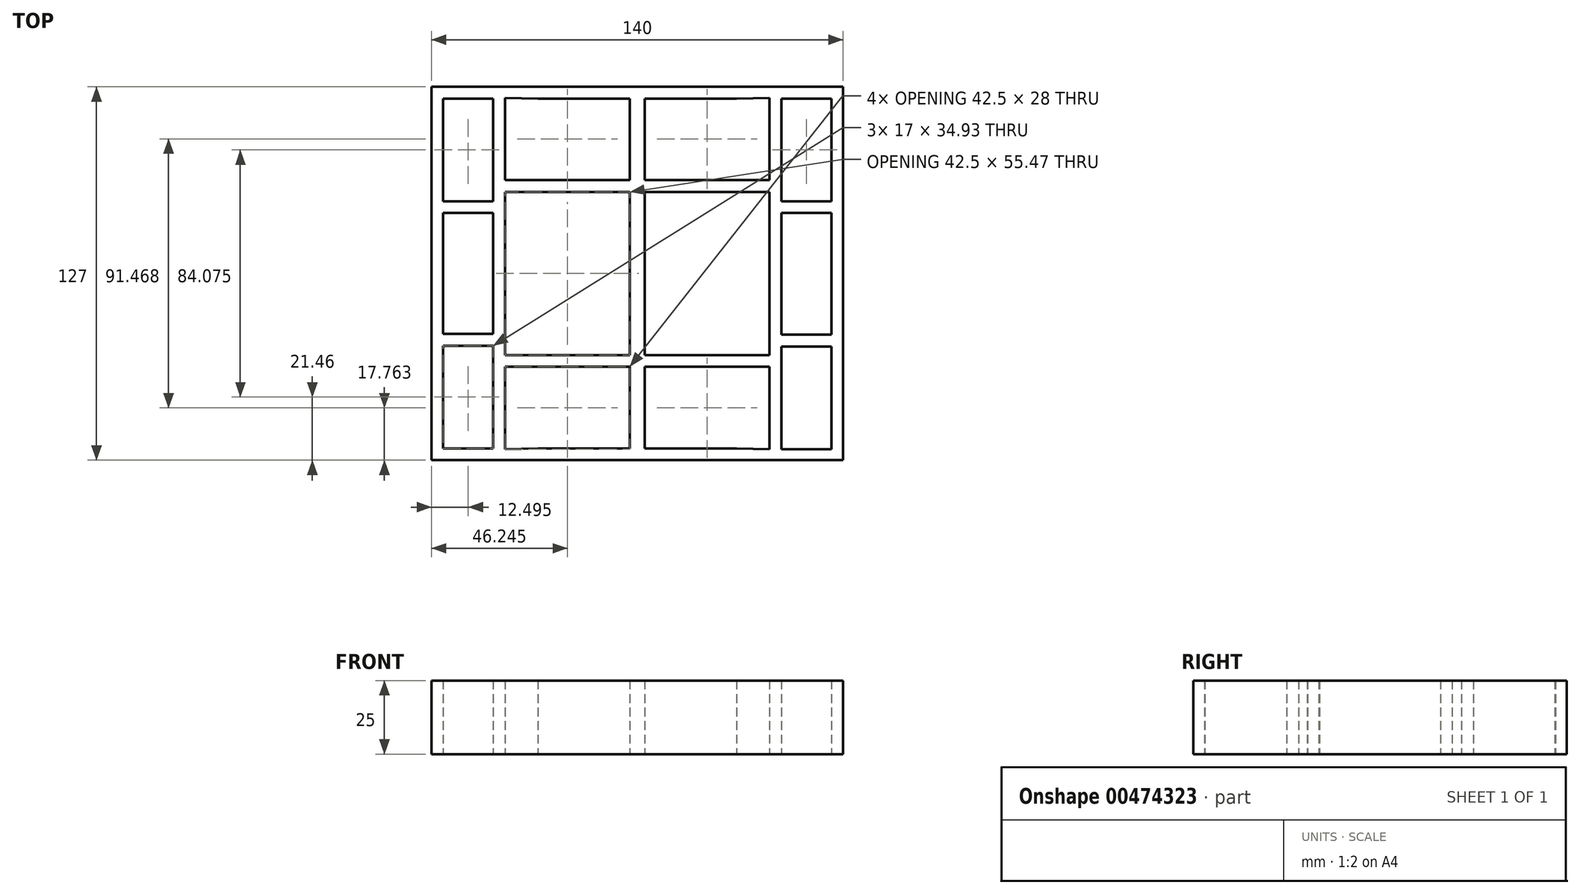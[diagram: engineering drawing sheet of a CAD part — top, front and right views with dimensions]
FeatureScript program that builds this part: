
annotation { "Feature Type Name" : "Feature", "Feature Type Description" : "" }
export const myFeature = defineFeature(function(context is Context, id is Id, definition is map)
    precondition{}
    {
        {
            var Q0;
            Q0=qCreatedBy(makeId("Top.planeOp"),FACE);
            var sketch = newSketch(context, id + "F0", { "sketchPlane" : qUnion([Q0])});
            skLineSegment(sketch, "E0", {"start": v(54.18, 45.65) * mm, "end": v(-85.82, 45.65) * mm});
            skLineSegment(sketch, "E1", {"start": v(-85.82, 45.65) * mm, "end": v(-85.82, -81.35) * mm});
            skLineSegment(sketch, "E2", {"start": v(54.18, -81.35) * mm, "end": v(-85.82, -81.35) * mm});
            skLineSegment(sketch, "E3", {"start": v(54.18, 45.65) * mm, "end": v(54.18, -81.35) * mm});
            skLineSegment(sketch, "E4", {"start": v(50.18, 41.65) * mm, "end": v(33.18, 41.65) * mm});
            skLineSegment(sketch, "E5", {"start": v(-81.82, -77.35) * mm, "end": v(-64.82, -77.35) * mm});
            skLineSegment(sketch, "E6", {"start": v(-81.82, 41.65) * mm, "end": v(-64.82, 41.65) * mm});
            skLineSegment(sketch, "E7", {"start": v(33.18, -77.59) * mm, "end": v(50.18, -77.59) * mm});
            skLineSegment(sketch, "E8", {"start": v(50.18, -10.85) * mm, "end": v(50.18, -24.85) * mm});
            skLineSegment(sketch, "E9", {"start": v(33.18, -10.85) * mm, "end": v(33.18, -24.85) * mm});
            skLineSegment(sketch, "E10", {"start": v(29.18, -10.85) * mm, "end": v(29.18, -24.85) * mm});
            skLineSegment(sketch, "E11", {"start": v(-13.32, -15.85) * mm, "end": v(-13.32, -19.85) * mm});
            skLineSegment(sketch, "E12", {"start": v(-18.32, -15.85) * mm, "end": v(-18.32, -19.85) * mm});
            skLineSegment(sketch, "E13", {"start": v(-60.82, -10.85) * mm, "end": v(-60.82, -24.85) * mm});
            skLineSegment(sketch, "E14", {"start": v(-64.82, -10.85) * mm, "end": v(-64.82, -24.85) * mm});
            skLineSegment(sketch, "E15", {"start": v(-81.82, -10.85) * mm, "end": v(-81.82, -24.85) * mm});
            skLineSegment(sketch, "E16", {"start": v(29.18, -77.59) * mm, "end": v(29.18, -49.59) * mm});
            skLineSegment(sketch, "E17", {"start": v(29.18, 41.88) * mm, "end": v(29.18, 13.88) * mm});
            skLineSegment(sketch, "E18", {"start": v(-60.82, 41.88) * mm, "end": v(-60.82, 13.88) * mm});
            skLineSegment(sketch, "E19", {"start": v(-60.82, -77.59) * mm, "end": v(-60.82, -49.59) * mm});
            skLineSegment(sketch, "E20", {"start": v(29.18, -49.59) * mm, "end": v(-13.32, -49.59) * mm});
            skLineSegment(sketch, "E21", {"start": v(29.18, -24.85) * mm, "end": v(29.18, -45.59) * mm});
            skLineSegment(sketch, "E22", {"start": v(29.18, -45.59) * mm, "end": v(-13.32, -45.59) * mm});
            skLineSegment(sketch, "E23", {"start": v(-13.32, -19.85) * mm, "end": v(-13.32, -45.59) * mm});
            skLineSegment(sketch, "E24", {"start": v(-13.32, -49.59) * mm, "end": v(-13.32, -61.31) * mm});
            skLineSegment(sketch, "E25", {"start": v(29.18, 13.88) * mm, "end": v(-13.32, 13.88) * mm});
            skLineSegment(sketch, "E26", {"start": v(29.18, 9.88) * mm, "end": v(-13.32, 9.88) * mm});
            skLineSegment(sketch, "E27", {"start": v(29.18, -10.85) * mm, "end": v(29.18, 9.88) * mm});
            skLineSegment(sketch, "E28", {"start": v(-13.32, -15.85) * mm, "end": v(-13.32, 9.88) * mm});
            skLineSegment(sketch, "E29", {"start": v(-13.32, 13.88) * mm, "end": v(-13.32, 25.6) * mm});
            skLineSegment(sketch, "E30", {"start": v(-60.82, 13.88) * mm, "end": v(-18.32, 13.88) * mm});
            skLineSegment(sketch, "E31", {"start": v(-60.82, 9.88) * mm, "end": v(-18.32, 9.88) * mm});
            skLineSegment(sketch, "E32", {"start": v(-60.82, -10.85) * mm, "end": v(-60.82, 9.88) * mm});
            skLineSegment(sketch, "E33", {"start": v(-60.82, -49.59) * mm, "end": v(-18.32, -49.59) * mm});
            skLineSegment(sketch, "E34", {"start": v(-60.82, -45.59) * mm, "end": v(-18.32, -45.59) * mm});
            skLineSegment(sketch, "E35", {"start": v(-60.82, -24.85) * mm, "end": v(-60.82, -45.59) * mm});
            skLineSegment(sketch, "E36", {"start": v(-18.32, 25.6) * mm, "end": v(-18.32, 13.88) * mm});
            skLineSegment(sketch, "E37", {"start": v(-18.32, 9.88) * mm, "end": v(-18.32, -15.85) * mm});
            skLineSegment(sketch, "E38", {"start": v(-18.32, -19.85) * mm, "end": v(-18.32, -45.59) * mm});
            skLineSegment(sketch, "E39", {"start": v(-18.32, -49.59) * mm, "end": v(-18.32, -61.31) * mm});
            skLineSegment(sketch, "E40", {"start": v(33.18, -42.66) * mm, "end": v(50.18, -42.66) * mm});
            skPoint(sketch, "E41.endSnap0", {"position": v(-73.32, -77.35) * mm});
            skLineSegment(sketch, "E42", {"start": v(50.18, 6.72) * mm, "end": v(33.18, 6.72) * mm});
            skLineSegment(sketch, "E43", {"start": v(-81.82, 6.72) * mm, "end": v(-64.82, 6.72) * mm});
            skLineSegment(sketch, "E44", {"start": v(-81.82, -42.43) * mm, "end": v(-64.82, -42.43) * mm});
            skLineSegment(sketch, "E45", {"start": v(-81.82, 2.72) * mm, "end": v(-64.82, 2.72) * mm});
            skLineSegment(sketch, "E46", {"start": v(-81.82, -38.43) * mm, "end": v(-64.82, -38.43) * mm});
            skLineSegment(sketch, "E47", {"start": v(33.18, 2.72) * mm, "end": v(50.18, 2.72) * mm});
            skLineSegment(sketch, "E48", {"start": v(33.18, -38.66) * mm, "end": v(50.18, -38.66) * mm});
            skLineSegment(sketch, "E49", {"start": v(33.18, -42.66) * mm, "end": v(33.18, -77.59) * mm});
            skLineSegment(sketch, "E50", {"start": v(50.18, -42.66) * mm, "end": v(50.18, -77.59) * mm});
            skLineSegment(sketch, "E51", {"start": v(33.18, -24.85) * mm, "end": v(33.18, -38.66) * mm});
            skLineSegment(sketch, "E52", {"start": v(50.18, -24.85) * mm, "end": v(50.18, -38.66) * mm});
            skLineSegment(sketch, "E53", {"start": v(33.18, 41.65) * mm, "end": v(33.18, 6.72) * mm});
            skLineSegment(sketch, "E54", {"start": v(33.18, 2.72) * mm, "end": v(33.18, -10.85) * mm});
            skLineSegment(sketch, "E55", {"start": v(50.18, 41.65) * mm, "end": v(50.18, 6.72) * mm});
            skLineSegment(sketch, "E56", {"start": v(50.18, 2.72) * mm, "end": v(50.18, -10.85) * mm});
            skLineSegment(sketch, "E57", {"start": v(-81.82, 41.65) * mm, "end": v(-81.82, 6.72) * mm});
            skLineSegment(sketch, "E58", {"start": v(-81.82, 2.72) * mm, "end": v(-81.82, -10.85) * mm});
            skLineSegment(sketch, "E59", {"start": v(-81.82, -24.85) * mm, "end": v(-81.82, -38.43) * mm});
            skLineSegment(sketch, "E60", {"start": v(-81.82, -42.43) * mm, "end": v(-81.82, -77.35) * mm});
            skLineSegment(sketch, "E61", {"start": v(-64.82, -77.35) * mm, "end": v(-64.82, -42.43) * mm});
            skLineSegment(sketch, "E62", {"start": v(-64.82, -38.43) * mm, "end": v(-64.82, -24.85) * mm});
            skLineSegment(sketch, "E63", {"start": v(-64.82, -10.85) * mm, "end": v(-64.82, 2.72) * mm});
            skLineSegment(sketch, "E64", {"start": v(-64.82, 6.72) * mm, "end": v(-64.82, 41.65) * mm});
            skLineSegment(sketch, "E65", {"start": v(-60.82, 41.88) * mm, "end": v(-49.58, 41.65) * mm});
            skLineSegment(sketch, "E66", {"start": v(17.93, 41.65) * mm, "end": v(29.18, 41.88) * mm});
            skLineSegment(sketch, "E67", {"start": v(-18.32, 25.6) * mm, "end": v(-18.32, 41.65) * mm});
            skLineSegment(sketch, "E68", {"start": v(-13.32, 25.6) * mm, "end": v(-13.32, 41.65) * mm});
            skLineSegment(sketch, "E69", {"start": v(-60.82, -77.59) * mm, "end": v(-49.58, -77.35) * mm});
            skLineSegment(sketch, "E70", {"start": v(17.93, -77.35) * mm, "end": v(29.18, -77.59) * mm});
            skLineSegment(sketch, "E71", {"start": v(-18.32, -77.35) * mm, "end": v(-18.32, -61.31) * mm});
            skLineSegment(sketch, "E72", {"start": v(-13.32, -61.31) * mm, "end": v(-13.32, -77.35) * mm});
            skLineSegment(sketch, "E73", {"start": v(-49.58, -77.35) * mm, "end": v(-18.32, -77.35) * mm});
            skLineSegment(sketch, "E74", {"start": v(-13.32, -77.35) * mm, "end": v(17.93, -77.35) * mm});
            skLineSegment(sketch, "E75", {"start": v(-49.58, 41.65) * mm, "end": v(-18.32, 41.65) * mm});
            skLineSegment(sketch, "E76", {"start": v(-13.32, 41.65) * mm, "end": v(17.93, 41.65) * mm});
            skSolve(sketch);
        }
        {
            var Q0;
            Q0 = qSketchRegion(id + "F0", true);
            extrude(context, id + "F1", {"entities" : qUnion([Q0]), "depth" : 25 * mm});
        }
    });
